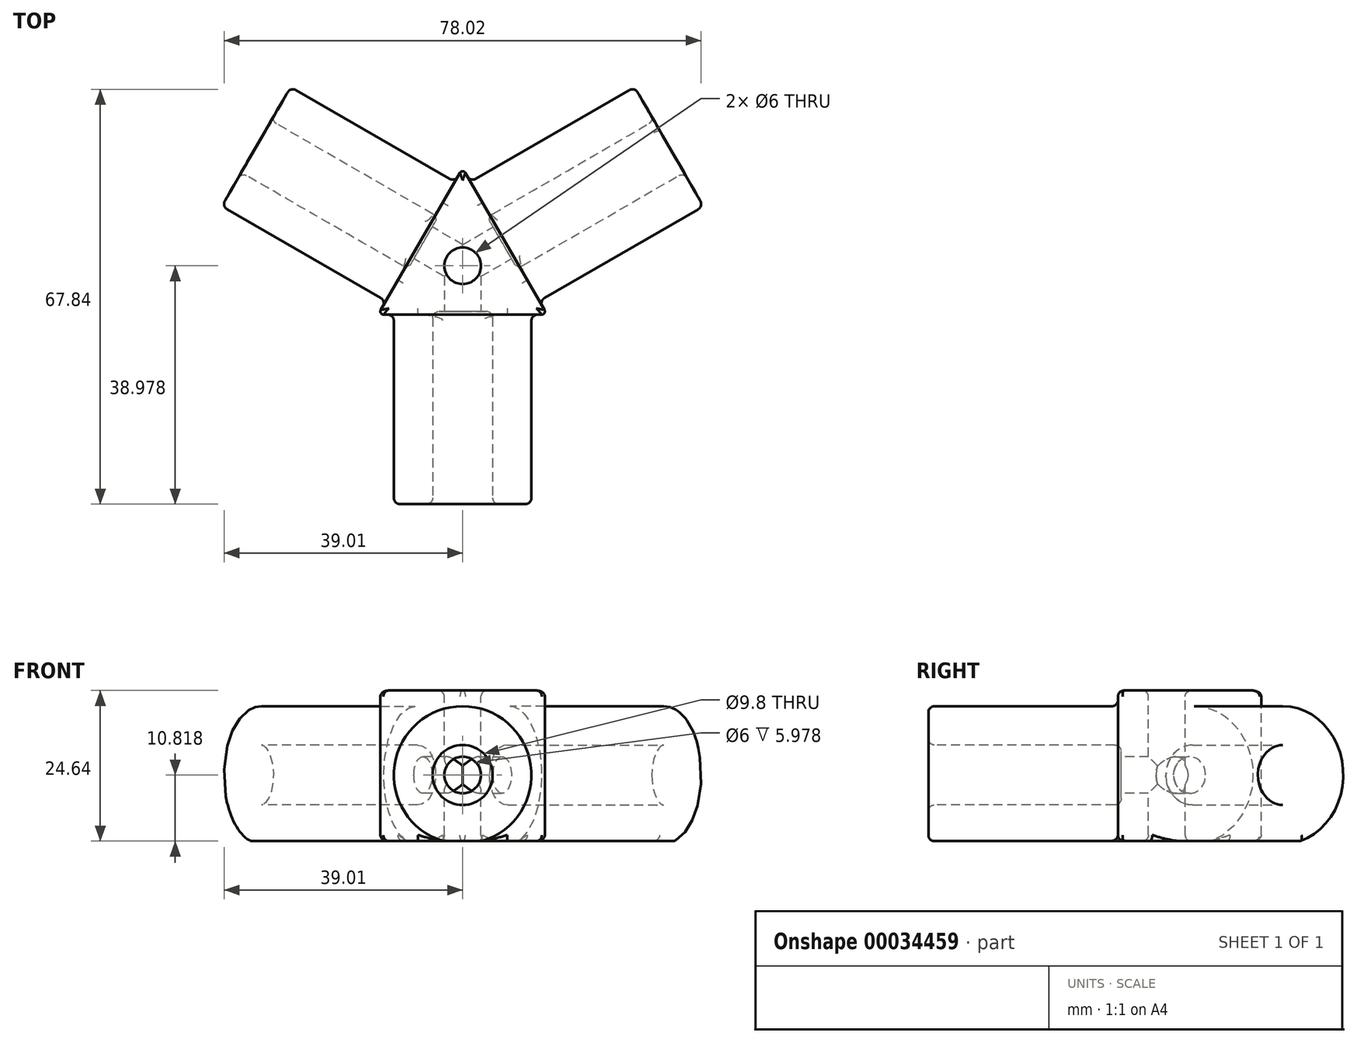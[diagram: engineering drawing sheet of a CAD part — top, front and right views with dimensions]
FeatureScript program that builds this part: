
annotation { "Feature Type Name" : "Feature", "Feature Type Description" : "" }
export const myFeature = defineFeature(function(context is Context, id is Id, definition is map)
    precondition{}
    {
        {
            var Q0;
            Q0=qCreatedBy(makeId("Top.planeOp"),FACE);
            var sketch = newSketch(context, id + "F0", { "sketchPlane" : qUnion([Q0])});
            skLineSegment(sketch, "E0", {"start": v(-13.82, 0) * mm, "end": v(13.82, 0) * mm});
            skLineSegment(sketch, "E1", {"start": v(0, 0) * mm, "end": v(0, 23.93) * mm, "construction": true});
            skLineSegment(sketch, "E2", {"start": v(0, 23.93) * mm, "end": v(-13.82, 0) * mm});
            skLineSegment(sketch, "E3", {"start": v(0, 23.93) * mm, "end": v(13.82, 0) * mm});
            skSolve(sketch);
        }
        {
            var Q0;
            Q0=makeQuery(id+"F0.imprint","IMPRINT",FACE,{"disambiguationData":[TD([[makeQuery(id+"F0.imprint","IMPRINT",EDGE,{"derivedFrom":sQuery(id+"F0.wireOp",EDGE,"E0")}),1.0]])]});
            extrude(context, id + "F1", {"entities" : qUnion([Q0]), "depth" : 27.64 * mm});
        }
        {
            var Q0;
            Q0=makeQuery(id+"F1.opExtrude","SWEPT_FACE",FACE,{"disambiguationData":[OSD([sQuery(id+"F0.wireOp",EDGE,"E2")])]});
            var sketch = newSketch(context, id + "F14", { "sketchPlane" : qUnion([Q0])});
            skLineSegment(sketch, "E4", {"start": v(-20.73, 27.64) * mm, "end": v(6.9, 0) * mm, "construction": true});
            skCircle(sketch, "E5", {"center": v(-6.9, 13.82) * mm, "radius": 11.25 * mm});
            skSolve(sketch);
        }
        {
            var Q0;
            Q0=qSketchRegion(id+"F14",true);
            extrude(context, id + "F2", {"entities" : qUnion([Q0]), "operationType" : NewBodyOperationType.ADD, "depth" : 31 * mm});
        }
        {
            var Q0;
            Q0=makeQuery(id+"F1.opExtrude","SWEPT_FACE",FACE,{"disambiguationData":[OSD([sQuery(id+"F0.wireOp",EDGE,"E0")])]});
            var sketch = newSketch(context, id + "F15", { "sketchPlane" : qUnion([Q0])});
            skLineSegment(sketch, "E6", {"start": v(-13.82, 27.64) * mm, "end": v(13.82, 0) * mm, "construction": true});
            skCircle(sketch, "E7", {"center": v(0, 13.82) * mm, "radius": 11.25 * mm});
            skSolve(sketch);
        }
        {
            var Q0;
            Q0=makeQuery(id+"F15.imprint","IMPRINT",FACE,{"disambiguationData":[TD([[makeQuery(id+"F15.imprint","IMPRINT",EDGE,{"derivedFrom":sQuery(id+"F15.wireOp",EDGE,"E7")}),1.0]])]});
            extrude(context, id + "F16", {"entities" : qUnion([Q0]), "operationType" : NewBodyOperationType.ADD, "depth" : 31 * mm});
        }
        {
            var Q0;
            Q0=makeQuery(id+"F1.opExtrude","SWEPT_FACE",FACE,{"disambiguationData":[OSD([sQuery(id+"F0.wireOp",EDGE,"E3")])]});
            var sketch = newSketch(context, id + "F3", { "sketchPlane" : qUnion([Q0])});
            skLineSegment(sketch, "E8", {"start": v(-6.9, 27.64) * mm, "end": v(20.73, 0) * mm, "construction": true});
            skCircle(sketch, "E9", {"center": v(6.9, 13.82) * mm, "radius": 11.25 * mm});
            skSolve(sketch);
        }
        {
            var Q0;
            Q0=makeQuery(id+"F3.imprint","IMPRINT",FACE,{"disambiguationData":[TD([[makeQuery(id+"F3.imprint","IMPRINT",EDGE,{"derivedFrom":sQuery(id+"F3.wireOp",EDGE,"E9")}),1.0]])]});
            extrude(context, id + "F4", {"entities" : qUnion([Q0]), "operationType" : NewBodyOperationType.ADD, "depth" : 31 * mm});
        }
        {
            var Q0;
            Q0=makeQuery(id+"F4.opExtrude","CAP_FACE",FACE,{"disambiguationData":[OSD([sQuery(id+"F3.wireOp",EDGE,"E9")])],"isStart":false});
            var sketch = newSketch(context, id + "F5", { "sketchPlane" : qUnion([Q0])});
            skCircle(sketch, "E10", {"center": v(6.9, 13.82) * mm, "radius": 4.9 * mm});
            skSolve(sketch);
        }
        {
            var Q0;
            Q0=makeQuery(id+"F2.opExtrude","CAP_FACE",FACE,{"disambiguationData":[OSD([sQuery(id+"F14.wireOp",EDGE,"E5")])],"isStart":false});
            var sketch = newSketch(context, id + "F17", { "sketchPlane" : qUnion([Q0])});
            skCircle(sketch, "E11", {"center": v(-6.9, 13.82) * mm, "radius": 4.9 * mm});
            skSolve(sketch);
        }
        {
            var Q0;
            Q0=makeQuery(id+"F16.opExtrude","CAP_FACE",FACE,{"disambiguationData":[OSD([sQuery(id+"F15.wireOp",EDGE,"E7")])],"isStart":false});
            var sketch = newSketch(context, id + "F6", { "sketchPlane" : qUnion([Q0])});
            skCircle(sketch, "E12", {"center": v(0, 13.82) * mm, "radius": 4.9 * mm});
            skSolve(sketch);
        }
        {
            var Q0;
            Q0=makeQuery(id+"F6.imprint","IMPRINT",FACE,{"disambiguationData":[TD([[makeQuery(id+"F6.imprint","IMPRINT",EDGE,{"derivedFrom":sQuery(id+"F6.wireOp",EDGE,"E12")}),1.0]])]});
            extrude(context, id + "F7", {"entities" : qUnion([Q0]), "operationType" : NewBodyOperationType.REMOVE, "oppositeDirection" : true, "depth" : 31.5 * mm});
        }
        {
            var Q0;
            Q0=makeQuery(id+"F5.imprint","IMPRINT",FACE,{"disambiguationData":[TD([[makeQuery(id+"F5.imprint","IMPRINT",EDGE,{"derivedFrom":sQuery(id+"F5.wireOp",EDGE,"E10")}),1.0]])]});
            extrude(context, id + "F18", {"entities" : qUnion([Q0]), "operationType" : NewBodyOperationType.REMOVE, "oppositeDirection" : true, "depth" : 31.5 * mm});
        }
        {
            var Q0;
            Q0=makeQuery(id+"F17.imprint","IMPRINT",FACE,{"disambiguationData":[TD([[makeQuery(id+"F17.imprint","IMPRINT",EDGE,{"derivedFrom":sQuery(id+"F17.wireOp",EDGE,"E11")}),1.0]])]});
            extrude(context, id + "F19", {"entities" : qUnion([Q0]), "operationType" : NewBodyOperationType.REMOVE, "oppositeDirection" : true, "depth" : 31.5 * mm});
        }
        {
            var Q0;
            Q0=makeQuery(id+"F1.opExtrude","CAP_FACE",FACE,{"disambiguationData":[OSD([sQuery(id+"F0.wireOp",EDGE,"E0"),sQuery(id+"F0.wireOp",EDGE,"E2"),sQuery(id+"F0.wireOp",EDGE,"E3")])],"isStart":false});
            var sketch = newSketch(context, id + "F20", { "sketchPlane" : qUnion([Q0])});
            skLineSegment(sketch, "E13", {"start": v(-13.82, 0) * mm, "end": v(6.9, 11.97) * mm, "construction": true});
            skLineSegment(sketch, "E14", {"start": v(0, 23.93) * mm, "end": v(0, 0) * mm, "construction": true});
            skLineSegment(sketch, "E15", {"start": v(13.82, 0) * mm, "end": v(-6.9, 11.97) * mm, "construction": true});
            skCircle(sketch, "E16", {"center": v(0, 7.98) * mm, "radius": 3 * mm});
            skSolve(sketch);
        }
        {
            var Q0;
            Q0=qSketchRegion(id+"F20",true);
            extrude(context, id + "F21", {"entities" : qUnion([Q0]), "operationType" : NewBodyOperationType.REMOVE, "endBound" : BoundingType.THROUGH_ALL, "oppositeDirection" : true, "depth" : 25.4 * mm});
        }
        {
            var Q0;
            Q0=qCreatedBy(makeId("Top.planeOp"),FACE);
            var sketch = newSketch(context, id + "F22", { "sketchPlane" : qUnion([Q0])});
            skCircle(sketch, "E17", {"center": v(0, 7.98) * mm, "radius": 41.28 * mm});
            skSolve(sketch);
        }
        {
            var Q0;
            Q0=makeQuery(id+"F22.imprint","IMPRINT",FACE,{"disambiguationData":[TD([[makeQuery(id+"F22.imprint","IMPRINT",EDGE,{"derivedFrom":sQuery(id+"F22.wireOp",EDGE,"E17")}),1.0]])]});
            extrude(context, id + "F8", {"entities" : qUnion([Q0]), "operationType" : NewBodyOperationType.REMOVE, "depth" : 3 * mm});
        }
        {
            var Q0;
            Q0=makeQuery(id+"F16.opExtrude","SWEPT_FACE",FACE,{"disambiguationData":[OSD([sQuery(id+"F15.wireOp",EDGE,"E7")])]});
            var Q1;
            Q1=makeQuery(id+"F4.opExtrude","SWEPT_FACE",FACE,{"disambiguationData":[OSD([sQuery(id+"F3.wireOp",EDGE,"E9")])]});
            var Q2;
            Q2=makeQuery(id+"F2.opExtrude","SWEPT_FACE",FACE,{"disambiguationData":[OSD([sQuery(id+"F14.wireOp",EDGE,"E5")])]});
            var Q3;
            Q3=makeQuery(id+"F2.opExtrude","CAP_FACE",FACE,{"disambiguationData":[OSD([sQuery(id+"F14.wireOp",EDGE,"E5")])],"isStart":false});
            var Q4;
            Q4=makeQuery(id+"F19.boolean.opBoolean","COPY",FACE,{"derivedFrom":makeQuery(id+"F19.opExtrude","SWEPT_FACE",FACE,{"disambiguationData":[OSD([sQuery(id+"F17.wireOp",EDGE,"E11")])]})});
            var Q5;
            Q5=makeQuery(id+"F7.boolean.opBoolean","COPY",FACE,{"derivedFrom":makeQuery(id+"F7.opExtrude","SWEPT_FACE",FACE,{"disambiguationData":[OSD([sQuery(id+"F6.wireOp",EDGE,"E12")])]})});
            var Q6;
            Q6=makeQuery(id+"F18.boolean.opBoolean","COPY",FACE,{"derivedFrom":makeQuery(id+"F18.opExtrude","SWEPT_FACE",FACE,{"disambiguationData":[OSD([sQuery(id+"F5.wireOp",EDGE,"E10")])]})});
            var Q7;
            Q7=makeQuery(id+"F21.boolean.opBoolean","COPY",FACE,{"derivedFrom":makeQuery(id+"F21.opExtrude","SWEPT_FACE",FACE,{"disambiguationData":[OSD([sQuery(id+"F20.wireOp",EDGE,"E16")])]})});
            var Q8;
            Q8=makeQuery(id+"F1.opExtrude","CAP_FACE",FACE,{"disambiguationData":[OSD([sQuery(id+"F0.wireOp",EDGE,"E0"),sQuery(id+"F0.wireOp",EDGE,"E2"),sQuery(id+"F0.wireOp",EDGE,"E3")])],"isStart":false});
            var Q9;
            Q9=makeQuery(id+"F8.boolean.opBoolean","INTERSECT",EDGE,{"disambiguationData":[OD(0.0)],"derivedFrom":[makeQuery(id+"F1.opExtrude","SWEPT_FACE",FACE,{"disambiguationData":[OSD([sQuery(id+"F0.wireOp",EDGE,"E3")])]}),makeQuery(id+"F8.opExtrude","CAP_FACE",FACE,{"disambiguationData":[OSD([sQuery(id+"F22.wireOp",EDGE,"E17")])],"isStart":false})]});
            var Q10;
            Q10=makeQuery(id+"F8.boolean.opBoolean","COPY",FACE,{"derivedFrom":makeQuery(id+"F8.opExtrude","CAP_FACE",FACE,{"disambiguationData":[OSD([sQuery(id+"F22.wireOp",EDGE,"E17")])],"isStart":false})});
            fillet(context, id + "F9", {"entities" : qUnion([Q0, Q1, Q2, Q3, Q4, Q5, Q6, Q7, Q8, Q9, Q10]), "radius" : 1 * mm, "tangentPropagation" : true, "allowEdgeOverflow" : false});
        }
        {
            var Q0;
            Q0=makeQuery(id+"F1.opExtrude","SWEPT_EDGE",EDGE,{"disambiguationData":[OSD([sQuery(id+"F0.wireOp",EDGE,"E2"),sQuery(id+"F0.wireOp",EDGE,"E3")])]});
            var Q1;
            Q1=makeQuery(id+"F1.opExtrude","SWEPT_EDGE",EDGE,{"disambiguationData":[OSD([sQuery(id+"F0.wireOp",EDGE,"E0"),sQuery(id+"F0.wireOp",EDGE,"E2")])]});
            var Q2;
            Q2=makeQuery(id+"F1.opExtrude","SWEPT_EDGE",EDGE,{"disambiguationData":[OSD([sQuery(id+"F0.wireOp",EDGE,"E0"),sQuery(id+"F0.wireOp",EDGE,"E3")])]});
            fillet(context, id + "F23", {"entities" : qUnion([Q0, Q1, Q2]), "radius" : 0.5 * mm, "tangentPropagation" : true, "allowEdgeOverflow" : false});
        }
        {
            var Q0;
            Q0=makeQuery(id+"F7.boolean.opBoolean","COPY",FACE,{"derivedFrom":makeQuery(id+"F7.opExtrude","CAP_FACE",FACE,{"disambiguationData":[OSD([sQuery(id+"F6.wireOp",EDGE,"E12")])],"isStart":false})});
            var sketch = newSketch(context, id + "F24", { "sketchPlane" : qUnion([Q0])});
            skCircle(sketch, "E18", {"center": v(0, 13.82) * mm, "radius": 3 * mm});
            skSolve(sketch);
        }
        {
            var Q0;
            Q0=qSketchRegion(id+"F24",true);
            extrude(context, id + "F25", {"entities" : qUnion([Q0]), "operationType" : NewBodyOperationType.REMOVE, "oppositeDirection" : true, "depth" : 8 * mm});
        }
        {
            var Q0;
            Q0=makeQuery(id+"F19.boolean.opBoolean","COPY",FACE,{"derivedFrom":makeQuery(id+"F19.opExtrude","CAP_FACE",FACE,{"disambiguationData":[OSD([sQuery(id+"F17.wireOp",EDGE,"E11")])],"isStart":false})});
            var sketch = newSketch(context, id + "F10", { "sketchPlane" : qUnion([Q0])});
            skCircle(sketch, "E19", {"center": v(-6.9, 13.82) * mm, "radius": 3 * mm});
            skSolve(sketch);
        }
        {
            var Q0;
            Q0=qSketchRegion(id+"F10",true);
            extrude(context, id + "F11", {"entities" : qUnion([Q0]), "operationType" : NewBodyOperationType.REMOVE, "oppositeDirection" : true, "depth" : 8 * mm});
        }
        {
            var Q0;
            Q0=makeQuery(id+"F18.boolean.opBoolean","COPY",FACE,{"derivedFrom":makeQuery(id+"F18.opExtrude","CAP_FACE",FACE,{"disambiguationData":[OSD([sQuery(id+"F5.wireOp",EDGE,"E10")])],"isStart":false})});
            var sketch = newSketch(context, id + "F12", { "sketchPlane" : qUnion([Q0])});
            skCircle(sketch, "E20", {"center": v(6.9, 13.82) * mm, "radius": 3 * mm});
            skSolve(sketch);
        }
        {
            var Q0;
            Q0=qSketchRegion(id+"F12",true);
            extrude(context, id + "F13", {"entities" : qUnion([Q0]), "operationType" : NewBodyOperationType.REMOVE, "oppositeDirection" : true, "depth" : 8 * mm});
        }
    });
